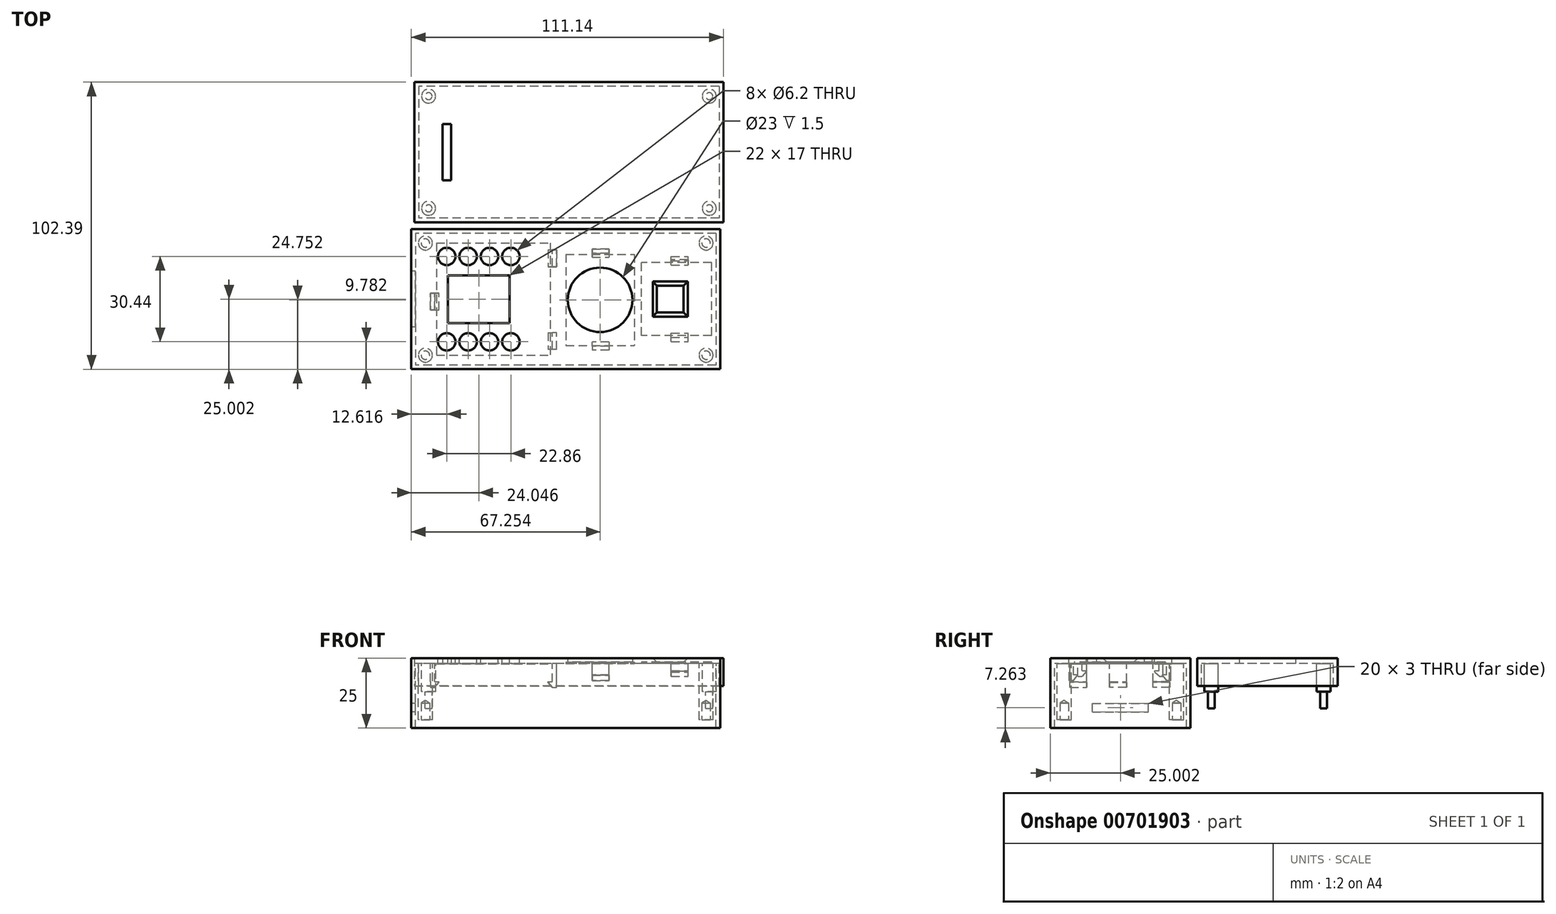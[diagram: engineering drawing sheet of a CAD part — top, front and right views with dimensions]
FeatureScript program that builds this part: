
annotation { "Feature Type Name" : "Feature", "Feature Type Description" : "" }
export const myFeature = defineFeature(function(context is Context, id is Id, definition is map)
    precondition{}
    {
        {
            var Q0;
            Q0=qCreatedBy(makeId("Top.planeOp"),FACE);
            var sketch = newSketch(context, id + "F0", { "sketchPlane" : qUnion([Q0])});
            skLineSegment(sketch, "E0.bottom", {"start": v(-49.7, 36.95) * mm, "end": v(60.3, 36.95) * mm});
            skLineSegment(sketch, "E0.top", {"start": v(-49.7, -13.05) * mm, "end": v(60.3, -13.05) * mm});
            skLineSegment(sketch, "E0.left", {"start": v(-49.7, 36.95) * mm, "end": v(-49.7, -13.05) * mm});
            skLineSegment(sketch, "E0.right", {"start": v(60.3, 36.95) * mm, "end": v(60.3, -13.05) * mm});
            skLineSegment(sketch, "E1.bottom", {"start": v(5.3, 27.95) * mm, "end": v(29.8, 27.95) * mm});
            skLineSegment(sketch, "E1.top", {"start": v(5.3, -4.55) * mm, "end": v(29.8, -4.55) * mm});
            skLineSegment(sketch, "E1.left", {"start": v(5.3, 27.95) * mm, "end": v(5.3, -4.55) * mm});
            skLineSegment(sketch, "E1.right", {"start": v(29.8, 27.95) * mm, "end": v(29.8, -4.55) * mm});
            skCircle(sketch, "E2", {"center": v(17.54, 11.7) * mm, "radius": 11.5 * mm});
            skLineSegment(sketch, "E3.top", {"start": v(38.3, 7.7) * mm, "end": v(46.8, 7.7) * mm});
            skLineSegment(sketch, "E4.bottom", {"start": v(38.3, 16.2) * mm, "end": v(46.8, 16.2) * mm});
            skLineSegment(sketch, "E4.left", {"start": v(38.3, 16.2) * mm, "end": v(38.3, 7.7) * mm});
            skLineSegment(sketch, "E4.right", {"start": v(46.8, 16.2) * mm, "end": v(46.8, 7.7) * mm});
            skPoint(sketch, "E5.orphan", {"position": v(-44.7, 36.95) * mm});
            skSolve(sketch);
        }
        {
            var Q0;
            Q0 = qSketchRegion(id + "F0", true);
            extrude(context, id + "F1", {"entities" : qUnion([Q0]), "depth" : 2 * mm, "offsetDistance" : 25 * mm});
        }
        {
            var Q0;
            Q0=qCreatedBy(makeId("Top.planeOp"),FACE);
            var sketch = newSketch(context, id + "F2", { "sketchPlane" : qUnion([Q0])});
            skLineSegment(sketch, "E6.bottom", {"start": v(-40.76, 31.95) * mm, "end": v(-0.26, 31.95) * mm});
            skLineSegment(sketch, "E6.top", {"start": v(-40.76, -8.05) * mm, "end": v(-0.26, -8.05) * mm});
            skLineSegment(sketch, "E6.left", {"start": v(-40.76, 31.95) * mm, "end": v(-40.76, -8.05) * mm});
            skLineSegment(sketch, "E6.right", {"start": v(-0.26, 31.95) * mm, "end": v(-0.26, -8.05) * mm});
            skCircle(sketch, "E7.MirrorC", {"center": v(-37.1, -3.27) * mm, "radius": 3.1 * mm});
            skLineSegment(sketch, "E8.bottom", {"start": v(-14.66, 20.45) * mm, "end": v(-14.66, 3.45) * mm});
            skLineSegment(sketch, "E8.top", {"start": v(-36.66, 20.45) * mm, "end": v(-36.66, 3.45) * mm});
            skLineSegment(sketch, "E8.left", {"start": v(-14.66, 20.45) * mm, "end": v(-36.66, 20.45) * mm});
            skLineSegment(sketch, "E8.right", {"start": v(-14.66, 3.45) * mm, "end": v(-36.66, 3.45) * mm});
            skPoint(sketch, "E9.orphan", {"position": v(-0.26, 11.95) * mm});
            skPoint(sketch, "E10.end.orphan", {"position": v(-40.76, 11.95) * mm});
            skCircle(sketch, "E11.1.0.0", {"center": v(-29.47, -3.27) * mm, "radius": 3.1 * mm});
            skCircle(sketch, "E11.2.0.0", {"center": v(-21.85, -3.27) * mm, "radius": 3.1 * mm});
            skCircle(sketch, "E11.3.0.0", {"center": v(-14.23, -3.27) * mm, "radius": 3.1 * mm});
            skLineSegment(sketch, "E11.direction1", {"start": v(-37.1, -3.27) * mm, "end": v(-29.47, -3.27) * mm, "construction": true});
            skCircle(sketch, "E12.MirrorC", {"center": v(-37.1, 27.17) * mm, "radius": 3.1 * mm});
            skCircle(sketch, "E13.1.0.0", {"center": v(-29.47, 27.17) * mm, "radius": 3.1 * mm});
            skCircle(sketch, "E13.2.0.0", {"center": v(-21.85, 27.17) * mm, "radius": 3.1 * mm});
            skCircle(sketch, "E13.3.0.0", {"center": v(-14.23, 27.17) * mm, "radius": 3.1 * mm});
            skLineSegment(sketch, "E13.direction1", {"start": v(-37.1, 27.17) * mm, "end": v(-29.47, 27.17) * mm, "construction": true});
            skSolve(sketch);
        }
        {
            var Q0;
            Q0 = qSketchRegion(id + "F2", true);
            extrude(context, id + "F3", {"entities" : qUnion([Q0]), "operationType" : NewBodyOperationType.ADD, "oppositeDirection" : true, "depth" : 0.1 * mm, "offsetDistance" : 25 * mm});
        }
        {
            var Q0;
            Q0=makeQuery(id+"F0.imprint","IMPRINT",FACE,{"disambiguationData":[TD([[makeQuery(id+"F0.imprint","IMPRINT",EDGE,{"derivedFrom":sQuery(id+"F0.wireOp",EDGE,"E1.bottom")}),-1.0]])]});
            extrude(context, id + "F4", {"entities" : qUnion([Q0]), "operationType" : NewBodyOperationType.ADD, "depth" : 2 * mm, "offsetDistance" : 25 * mm});
        }
        {
            var Q0;
            Q0=makeQuery(id+"F2.imprint","IMPRINT",FACE,{"disambiguationData":[TD([[makeQuery(id+"F2.imprint","IMPRINT",EDGE,{"derivedFrom":sQuery(id+"F2.wireOp",EDGE,"E8.bottom")}),-1.0]])]});
            extrude(context, id + "F5", {"entities" : qUnion([Q0]), "operationType" : NewBodyOperationType.REMOVE, "oppositeDirection" : true, "depth" : 5 * mm, "offsetDistance" : 25 * mm});
        }
        {
            var Q0;
            {var subQ0=sQuery(id+"F0.wireOp",EDGE,"E3.right");var subQ1=sQuery(id+"F0.wireOp",EDGE,"E3.left");var subQ2=sQuery(id+"F0.wireOp",EDGE,"E3.bottom");var subQ3=sQuery(id+"F0.wireOp",EDGE,"E1.right");var subQ4=sQuery(id+"F0.wireOp",EDGE,"E1.left");var subQ5=sQuery(id+"F0.wireOp",EDGE,"E1.top");var subQ6=sQuery(id+"F0.wireOp",EDGE,"E1.bottom");Q0=makeQuery(id+"FzuolDucDf3GuWk_4.boolean.opBoolean","MERGE",FACE,{"derivedFrom":[makeQuery(id+"F4.boolean.opBoolean","MERGE",FACE,{"derivedFrom":[makeQuery(id+"F1.opExtrude","CAP_FACE",FACE,{"disambiguationData":[OSD([sQuery(id+"F0.wireOp",EDGE,"E0.bottom"),sQuery(id+"F0.wireOp",EDGE,"E0.top"),sQuery(id+"F0.wireOp",EDGE,"E0.left"),sQuery(id+"F0.wireOp",EDGE,"E0.right"),subQ6,subQ5,subQ4,subQ3,subQ2,subQ1,subQ0,sQuery(id+"F0.wireOp",EDGE,"E3.top"),sQuery(id+"F0.wireOp",EDGE,"E4.left"),sQuery(id+"F0.wireOp",EDGE,"E4.right")])],"isStart":true}),makeQuery(id+"F4.opExtrude","CAP_FACE",FACE,{"disambiguationData":[OSD([subQ6,subQ5,subQ4,subQ3,sQuery(id+"F0.wireOp",EDGE,"E2")])],"isStart":true})]}),makeQuery(id+"FzuolDucDf3GuWk_4.opExtrude","CAP_FACE",FACE,{"disambiguationData":[OSD([subQ2,subQ1,subQ0,sQuery(id+"F0.wireOp",EDGE,"E4.bottom")])],"isStart":true})]});}
            var sketch = newSketch(context, id + "F6", { "sketchPlane" : qUnion([Q0])});
            skLineSegment(sketch, "E14.bottom", {"start": v(60.3, -36.95) * mm, "end": v(58.8, -36.95) * mm});
            skLineSegment(sketch, "E14.top", {"start": v(60.3, 13.05) * mm, "end": v(58.8, 13.05) * mm});
            skLineSegment(sketch, "E14.left", {"start": v(60.3, -36.95) * mm, "end": v(60.3, 13.05) * mm});
            skLineSegment(sketch, "E14.right", {"start": v(58.8, -36.95) * mm, "end": v(58.8, 13.05) * mm});
            skLineSegment(sketch, "E15.bottom", {"start": v(-49.7, -36.95) * mm, "end": v(-48.2, -36.95) * mm});
            skLineSegment(sketch, "E15.top", {"start": v(-49.7, 13.05) * mm, "end": v(-48.2, 13.05) * mm});
            skLineSegment(sketch, "E15.left", {"start": v(-49.7, -36.95) * mm, "end": v(-49.7, 13.05) * mm});
            skLineSegment(sketch, "E15.right", {"start": v(-48.2, -36.95) * mm, "end": v(-48.2, 13.05) * mm});
            skLineSegment(sketch, "E16.bottom", {"start": v(58.8, -36.95) * mm, "end": v(-48.2, -36.95) * mm});
            skLineSegment(sketch, "E16.top", {"start": v(58.8, -35.45) * mm, "end": v(-48.2, -35.45) * mm});
            skLineSegment(sketch, "E16.left", {"start": v(58.8, -36.95) * mm, "end": v(58.8, -35.45) * mm});
            skLineSegment(sketch, "E16.right", {"start": v(-48.2, -36.95) * mm, "end": v(-48.2, -35.45) * mm});
            skLineSegment(sketch, "E17.bottom", {"start": v(58.8, 13.05) * mm, "end": v(-48.2, 13.05) * mm});
            skLineSegment(sketch, "E17.top", {"start": v(58.8, 11.55) * mm, "end": v(-48.2, 11.55) * mm});
            skLineSegment(sketch, "E17.left", {"start": v(58.8, 13.05) * mm, "end": v(58.8, 11.55) * mm});
            skLineSegment(sketch, "E17.right", {"start": v(-48.2, 13.05) * mm, "end": v(-48.2, 11.55) * mm});
            skSolve(sketch);
        }
        {
            var Q0;
            Q0 = qSketchRegion(id + "F6", true);
            extrude(context, id + "F7", {"entities" : qUnion([Q0]), "operationType" : NewBodyOperationType.ADD, "depth" : 23 * mm, "offsetDistance" : 25 * mm});
        }
        {
            var Q0;
            Q0 = qSketchRegion(id + "F6", true);
            extrude(context, id + "F8", {"entities" : qUnion([Q0]), "operationType" : NewBodyOperationType.ADD, "depth" : 10 * mm, "offsetDistance" : 25 * mm});
        }
        {
            var Q0;
            Q0 = qSketchRegion(id + "F6", true);
            extrude(context, id + "F9", {"entities" : qUnion([Q0]), "operationType" : NewBodyOperationType.ADD, "depth" : 10 * mm, "offsetDistance" : 25 * mm});
        }
        {
            var Q0;
            Q0 = qSketchRegion(id + "F6", true);
            extrude(context, id + "F10", {"entities" : qUnion([Q0]), "operationType" : NewBodyOperationType.ADD, "depth" : 10 * mm, "offsetDistance" : 25 * mm});
        }
        {
            var Q0;
            {var subQ0=sQuery(id+"F0.wireOp",EDGE,"E3.right");var subQ1=sQuery(id+"F0.wireOp",EDGE,"E3.left");var subQ2=sQuery(id+"F0.wireOp",EDGE,"E3.bottom");var subQ3=sQuery(id+"F0.wireOp",EDGE,"E1.right");var subQ4=sQuery(id+"F0.wireOp",EDGE,"E1.left");var subQ5=sQuery(id+"F0.wireOp",EDGE,"E1.top");var subQ6=sQuery(id+"F0.wireOp",EDGE,"E1.bottom");Q0=makeQuery(id+"FzuolDucDf3GuWk_4.boolean.opBoolean","MERGE",FACE,{"derivedFrom":[makeQuery(id+"F4.boolean.opBoolean","MERGE",FACE,{"derivedFrom":[makeQuery(id+"F1.opExtrude","CAP_FACE",FACE,{"disambiguationData":[OSD([sQuery(id+"F0.wireOp",EDGE,"E0.bottom"),sQuery(id+"F0.wireOp",EDGE,"E0.top"),sQuery(id+"F0.wireOp",EDGE,"E0.left"),sQuery(id+"F0.wireOp",EDGE,"E0.right"),subQ6,subQ5,subQ4,subQ3,subQ2,subQ1,subQ0,sQuery(id+"F0.wireOp",EDGE,"E3.top"),sQuery(id+"F0.wireOp",EDGE,"E4.left"),sQuery(id+"F0.wireOp",EDGE,"E4.right")])],"isStart":true}),makeQuery(id+"F4.opExtrude","CAP_FACE",FACE,{"disambiguationData":[OSD([subQ6,subQ5,subQ4,subQ3,sQuery(id+"F0.wireOp",EDGE,"E2")])],"isStart":true})]}),makeQuery(id+"FzuolDucDf3GuWk_4.opExtrude","CAP_FACE",FACE,{"disambiguationData":[OSD([subQ2,subQ1,subQ0,sQuery(id+"F0.wireOp",EDGE,"E4.bottom")])],"isStart":true})]});}
            var sketch = newSketch(context, id + "F11", { "sketchPlane" : qUnion([Q0])});
            skLineSegment(sketch, "E18.bottom", {"start": v(42.85, -25.68) * mm, "end": v(48.85, -25.68) * mm});
            skLineSegment(sketch, "E18.top", {"start": v(42.85, -27.18) * mm, "end": v(48.85, -27.18) * mm});
            skLineSegment(sketch, "E18.left", {"start": v(42.85, -25.68) * mm, "end": v(42.85, -27.18) * mm});
            skLineSegment(sketch, "E18.right", {"start": v(48.85, -25.68) * mm, "end": v(48.85, -27.18) * mm});
            skLineSegment(sketch, "E19.bottom", {"start": v(14.73, -28.35) * mm, "end": v(20.73, -28.35) * mm});
            skLineSegment(sketch, "E19.top", {"start": v(14.73, -29.85) * mm, "end": v(20.73, -29.85) * mm});
            skLineSegment(sketch, "E19.left", {"start": v(14.73, -28.35) * mm, "end": v(14.73, -29.85) * mm});
            skLineSegment(sketch, "E19.right", {"start": v(20.73, -28.35) * mm, "end": v(20.73, -29.85) * mm});
            skLineSegment(sketch, "E20.bottom", {"start": v(42.85, 3.2) * mm, "end": v(48.85, 3.2) * mm});
            skLineSegment(sketch, "E20.top", {"start": v(42.85, 1.7) * mm, "end": v(48.85, 1.7) * mm});
            skLineSegment(sketch, "E20.left", {"start": v(42.85, 3.2) * mm, "end": v(42.85, 1.7) * mm});
            skLineSegment(sketch, "E20.right", {"start": v(48.85, 3.2) * mm, "end": v(48.85, 1.7) * mm});
            skSolve(sketch);
        }
        {
            var Q0;
            Q0=makeQuery(id+"F11.imprint","IMPRINT",FACE,{"disambiguationData":[TD([[makeQuery(id+"F11.imprint","IMPRINT",EDGE,{"derivedFrom":sQuery(id+"F11.wireOp",EDGE,"E18.bottom")}),-1.0]])]});
            extrude(context, id + "F12", {"entities" : qUnion([Q0]), "operationType" : NewBodyOperationType.ADD, "depth" : 2.5 * mm, "offsetDistance" : 25 * mm});
        }
        {
            var Q0;
            Q0=makeQuery(id+"F11.imprint","IMPRINT",FACE,{"disambiguationData":[TD([[makeQuery(id+"F11.imprint","IMPRINT",EDGE,{"derivedFrom":sQuery(id+"F11.wireOp",EDGE,"E19.bottom")}),-1.0]])]});
            extrude(context, id + "F13", {"entities" : qUnion([Q0]), "operationType" : NewBodyOperationType.ADD, "depth" : 4 * mm, "offsetDistance" : 25 * mm});
        }
        {
            var Q0;
            Q0=makeQuery(id+"F13.opExtrude","CAP_FACE",FACE,{"disambiguationData":[OSD([sQuery(id+"F11.wireOp",EDGE,"E19.bottom"),sQuery(id+"F11.wireOp",EDGE,"E19.top"),sQuery(id+"F11.wireOp",EDGE,"E19.left"),sQuery(id+"F11.wireOp",EDGE,"E19.right")])],"isStart":false});
            var sketch = newSketch(context, id + "F14", { "sketchPlane" : qUnion([Q0])});
            skLineSegment(sketch, "E21.bottom", {"start": v(14.73, -29.85) * mm, "end": v(20.73, -29.85) * mm});
            skLineSegment(sketch, "E21.top", {"start": v(14.73, -26.85) * mm, "end": v(20.73, -26.85) * mm});
            skLineSegment(sketch, "E21.left", {"start": v(14.73, -29.85) * mm, "end": v(14.73, -26.85) * mm});
            skLineSegment(sketch, "E21.right", {"start": v(20.73, -29.85) * mm, "end": v(20.73, -26.85) * mm});
            skSolve(sketch);
        }
        {
            var Q0;
            Q0 = qSketchRegion(id + "F14", true);
            extrude(context, id + "F15", {"entities" : qUnion([Q0]), "operationType" : NewBodyOperationType.ADD, "depth" : 2 * mm, "offsetDistance" : 25 * mm});
        }
        {
            var Q0;
            Q0=makeQuery(id+"F15.opExtrude","CAP_EDGE",EDGE,{"disambiguationData":[OSD([sQuery(id+"F14.wireOp",EDGE,"E21.top")])],"isStart":false});
            chamfer(context, id + "F16", {"entities" : qUnion([Q0]), "chamferType" : ChamferType.OFFSET_ANGLE, "width" : 1.5 * mm, "oppositeDirection" : true, "angle" : 50 * degree, "tangentPropagation" : true});
        }
        {
            var Q0;
            Q0=makeQuery(id+"F11.imprint","IMPRINT",FACE,{"disambiguationData":[TD([[makeQuery(id+"F11.imprint","IMPRINT",EDGE,{"derivedFrom":sQuery(id+"F11.wireOp",EDGE,"E18.bottom")}),1.0]])]});
            var sketch = newSketch(context, id + "F17", { "sketchPlane" : qUnion([Q0])});
            skLineSegment(sketch, "E22.bottom", {"start": v(2.04, 6) * mm, "end": v(2.04, 0) * mm});
            skLineSegment(sketch, "E22.top", {"start": v(0.54, 6) * mm, "end": v(0.54, 0) * mm});
            skLineSegment(sketch, "E22.left", {"start": v(2.04, 6) * mm, "end": v(0.54, 6) * mm});
            skLineSegment(sketch, "E22.right", {"start": v(2.04, 0) * mm, "end": v(0.54, 0) * mm});
            skLineSegment(sketch, "E23.bottom", {"start": v(20.72, 4.8) * mm, "end": v(14.72, 4.8) * mm});
            skLineSegment(sketch, "E23.top", {"start": v(20.72, 6.3) * mm, "end": v(14.72, 6.3) * mm});
            skLineSegment(sketch, "E23.left", {"start": v(20.72, 4.8) * mm, "end": v(20.72, 6.3) * mm});
            skLineSegment(sketch, "E23.right", {"start": v(14.72, 4.8) * mm, "end": v(14.72, 6.3) * mm});
            skLineSegment(sketch, "E24.bottom", {"start": v(-41.42, -8.1) * mm, "end": v(-41.42, -14.1) * mm});
            skLineSegment(sketch, "E24.top", {"start": v(-42.92, -8.1) * mm, "end": v(-42.92, -14.1) * mm});
            skLineSegment(sketch, "E24.left", {"start": v(-41.42, -8.1) * mm, "end": v(-42.92, -8.1) * mm});
            skLineSegment(sketch, "E24.right", {"start": v(-41.42, -14.1) * mm, "end": v(-42.92, -14.1) * mm});
            skLineSegment(sketch, "E25.top", {"start": v(20.67, 4.85) * mm, "end": v(14.67, 4.85) * mm});
            skLineSegment(sketch, "E26.top", {"start": v(20.76, 4.8) * mm, "end": v(14.76, 4.8) * mm});
            skLineSegment(sketch, "E27.bottom", {"start": v(2.04, -23.5) * mm, "end": v(2.04, -29.5) * mm});
            skLineSegment(sketch, "E27.top", {"start": v(0.54, -23.5) * mm, "end": v(0.54, -29.5) * mm});
            skLineSegment(sketch, "E27.left", {"start": v(2.04, -23.5) * mm, "end": v(0.54, -23.5) * mm});
            skLineSegment(sketch, "E27.right", {"start": v(2.04, -29.5) * mm, "end": v(0.54, -29.5) * mm});
            skSolve(sketch);
        }
        {
            var Q0;
            Q0=makeQuery(id+"F17.imprint","IMPRINT",FACE,{"disambiguationData":[TD([[makeQuery(id+"F17.imprint","IMPRINT",EDGE,{"derivedFrom":sQuery(id+"F17.wireOp",EDGE,"E22.bottom")}),-1.0]])]});
            extrude(context, id + "F18", {"entities" : qUnion([Q0]), "operationType" : NewBodyOperationType.ADD, "depth" : 6.5 * mm, "offsetDistance" : 25 * mm});
        }
        {
            var Q0;
            Q0=makeQuery(id+"F17.imprint","IMPRINT",FACE,{"disambiguationData":[TD([[makeQuery(id+"F17.imprint","IMPRINT",EDGE,{"derivedFrom":sQuery(id+"F17.wireOp",EDGE,"E24.bottom")}),-1.0]])]});
            extrude(context, id + "F19", {"entities" : qUnion([Q0]), "operationType" : NewBodyOperationType.ADD, "depth" : 6.5 * mm, "offsetDistance" : 25 * mm});
        }
        {
            var Q0;
            {var subQ0=sQuery(id+"F17.wireOp",EDGE,"E23.left");Q0=makeQuery(id+"F17.imprint","IMPRINT",FACE,{"disambiguationData":[TD([[makeQuery(id+"F17.imprint","IMPRINT",EDGE,{"derivedFrom":subQ0}),1.0]])]});}
            extrude(context, id + "F20", {"entities" : qUnion([Q0]), "operationType" : NewBodyOperationType.ADD, "depth" : 4 * mm, "offsetDistance" : 25 * mm});
        }
        {
            var Q0;
            Q0=makeQuery(id+"F20.opExtrude","CAP_FACE",FACE,{"disambiguationData":[OSD([sQuery(id+"F17.wireOp",EDGE,"E23.bottom"),sQuery(id+"F17.wireOp",EDGE,"E23.top"),sQuery(id+"F17.wireOp",EDGE,"E23.left"),sQuery(id+"F17.wireOp",EDGE,"E26.right")])],"isStart":false});
            var sketch = newSketch(context, id + "F21", { "sketchPlane" : qUnion([Q0])});
            skLineSegment(sketch, "E28.bottom", {"start": v(20.72, 3.3) * mm, "end": v(20.72, 6.3) * mm});
            skLineSegment(sketch, "E28.top", {"start": v(14.72, 3.3) * mm, "end": v(14.72, 6.3) * mm});
            skLineSegment(sketch, "E28.left", {"start": v(20.72, 3.3) * mm, "end": v(14.72, 3.3) * mm});
            skLineSegment(sketch, "E28.right", {"start": v(20.72, 6.3) * mm, "end": v(14.72, 6.3) * mm});
            skSolve(sketch);
        }
        {
            var Q0;
            Q0 = qSketchRegion(id + "F21", true);
            extrude(context, id + "F22", {"entities" : qUnion([Q0]), "operationType" : NewBodyOperationType.ADD, "depth" : 2 * mm, "offsetDistance" : 25 * mm});
        }
        {
            var Q0;
            Q0=makeQuery(id+"F22.opExtrude","CAP_EDGE",EDGE,{"disambiguationData":[OSD([sQuery(id+"F21.wireOp",EDGE,"E28.left")])],"isStart":false});
            chamfer(context, id + "F23", {"entities" : qUnion([Q0]), "chamferType" : ChamferType.OFFSET_ANGLE, "width" : 1.5 * mm, "oppositeDirection" : true, "angle" : 50 * degree, "tangentPropagation" : true});
        }
        {
            var Q0;
            Q0=makeQuery(id+"F18.opExtrude","CAP_FACE",FACE,{"disambiguationData":[OSD([sQuery(id+"F17.wireOp",EDGE,"E22.bottom"),sQuery(id+"F17.wireOp",EDGE,"E22.top"),sQuery(id+"F17.wireOp",EDGE,"E22.left"),sQuery(id+"F17.wireOp",EDGE,"E22.right")])],"isStart":false});
            var sketch = newSketch(context, id + "F24", { "sketchPlane" : qUnion([Q0])});
            skLineSegment(sketch, "E29.bottom", {"start": v(-0.96, 0) * mm, "end": v(2.04, 0) * mm});
            skLineSegment(sketch, "E29.top", {"start": v(-0.96, 6) * mm, "end": v(2.04, 6) * mm});
            skLineSegment(sketch, "E29.left", {"start": v(-0.96, 0) * mm, "end": v(-0.96, 6) * mm});
            skLineSegment(sketch, "E29.right", {"start": v(2.04, 0) * mm, "end": v(2.04, 6) * mm});
            skSolve(sketch);
        }
        {
            var Q0;
            Q0 = qSketchRegion(id + "F24", true);
            extrude(context, id + "F25", {"entities" : qUnion([Q0]), "operationType" : NewBodyOperationType.ADD, "depth" : 2 * mm, "offsetDistance" : 25 * mm});
        }
        {
            var Q0;
            Q0=makeQuery(id+"F25.opExtrude","CAP_EDGE",EDGE,{"disambiguationData":[OSD([sQuery(id+"F24.wireOp",EDGE,"E29.left")])],"isStart":false});
            chamfer(context, id + "F26", {"entities" : qUnion([Q0]), "chamferType" : ChamferType.OFFSET_ANGLE, "width" : 1.5 * mm, "oppositeDirection" : true, "angle" : 50 * degree, "tangentPropagation" : true});
        }
        {
            var Q0;
            Q0=makeQuery(id+"F19.opExtrude","CAP_FACE",FACE,{"disambiguationData":[OSD([sQuery(id+"F17.wireOp",EDGE,"E24.bottom"),sQuery(id+"F17.wireOp",EDGE,"E24.top"),sQuery(id+"F17.wireOp",EDGE,"E24.left"),sQuery(id+"F17.wireOp",EDGE,"E24.right")])],"isStart":false});
            var sketch = newSketch(context, id + "F27", { "sketchPlane" : qUnion([Q0])});
            skLineSegment(sketch, "E30.bottom", {"start": v(-42.92, -14.1) * mm, "end": v(-39.92, -14.1) * mm});
            skLineSegment(sketch, "E30.top", {"start": v(-42.92, -8.1) * mm, "end": v(-39.92, -8.1) * mm});
            skLineSegment(sketch, "E30.left", {"start": v(-42.92, -14.1) * mm, "end": v(-42.92, -8.1) * mm});
            skLineSegment(sketch, "E30.right", {"start": v(-39.92, -14.1) * mm, "end": v(-39.92, -8.1) * mm});
            skSolve(sketch);
        }
        {
            var Q0;
            Q0 = qSketchRegion(id + "F27", true);
            extrude(context, id + "F28", {"entities" : qUnion([Q0]), "operationType" : NewBodyOperationType.ADD, "depth" : 2 * mm, "offsetDistance" : 25 * mm});
        }
        {
            var Q0;
            Q0=makeQuery(id+"F28.opExtrude","CAP_EDGE",EDGE,{"disambiguationData":[OSD([sQuery(id+"F27.wireOp",EDGE,"E30.right")])],"isStart":false});
            chamfer(context, id + "F29", {"entities" : qUnion([Q0]), "chamferType" : ChamferType.OFFSET_ANGLE, "width" : 1.5 * mm, "oppositeDirection" : false, "angle" : 50 * degree, "tangentPropagation" : true});
        }
        {
            var Q0;
            {var subQ0=sQuery(id+"F0.wireOp",EDGE,"E3.right");var subQ1=sQuery(id+"F0.wireOp",EDGE,"E3.left");var subQ2=sQuery(id+"F0.wireOp",EDGE,"E3.bottom");var subQ3=sQuery(id+"F0.wireOp",EDGE,"E1.right");var subQ4=sQuery(id+"F0.wireOp",EDGE,"E1.left");var subQ5=sQuery(id+"F0.wireOp",EDGE,"E1.top");var subQ6=sQuery(id+"F0.wireOp",EDGE,"E1.bottom");Q0=makeQuery(id+"FzuolDucDf3GuWk_4.boolean.opBoolean","MERGE",FACE,{"derivedFrom":[makeQuery(id+"F4.boolean.opBoolean","MERGE",FACE,{"derivedFrom":[makeQuery(id+"F1.opExtrude","CAP_FACE",FACE,{"disambiguationData":[OSD([sQuery(id+"F0.wireOp",EDGE,"E0.bottom"),sQuery(id+"F0.wireOp",EDGE,"E0.top"),sQuery(id+"F0.wireOp",EDGE,"E0.left"),sQuery(id+"F0.wireOp",EDGE,"E0.right"),subQ6,subQ5,subQ4,subQ3,subQ2,subQ1,subQ0,sQuery(id+"F0.wireOp",EDGE,"E3.top"),sQuery(id+"F0.wireOp",EDGE,"E4.left"),sQuery(id+"F0.wireOp",EDGE,"E4.right")])],"isStart":true}),makeQuery(id+"F4.opExtrude","CAP_FACE",FACE,{"disambiguationData":[OSD([subQ6,subQ5,subQ4,subQ3,sQuery(id+"F0.wireOp",EDGE,"E2")])],"isStart":true})]}),makeQuery(id+"FzuolDucDf3GuWk_4.opExtrude","CAP_FACE",FACE,{"disambiguationData":[OSD([subQ2,subQ1,subQ0,sQuery(id+"F0.wireOp",EDGE,"E4.bottom")])],"isStart":true})]});}
            var sketch = newSketch(context, id + "F30", { "sketchPlane" : qUnion([Q0])});
            skCircle(sketch, "E31", {"center": v(-44.7, 8.05) * mm, "radius": 2.5 * mm});
            skCircle(sketch, "E32", {"center": v(-44.7, -31.95) * mm, "radius": 2.5 * mm});
            skCircle(sketch, "E33", {"center": v(55.3, -31.95) * mm, "radius": 2.5 * mm});
            skCircle(sketch, "E34", {"center": v(55.3, 8.05) * mm, "radius": 2.5 * mm});
            skSolve(sketch);
        }
        {
            var Q0;
            Q0=makeQuery(id+"F30.imprint","IMPRINT",FACE,{"disambiguationData":[TD([[makeQuery(id+"F30.imprint","IMPRINT",EDGE,{"derivedFrom":sQuery(id+"F30.wireOp",EDGE,"E31")}),1.0]])]});
            var Q1;
            Q1=makeQuery(id+"F30.imprint","IMPRINT",FACE,{"disambiguationData":[TD([[makeQuery(id+"F30.imprint","IMPRINT",EDGE,{"derivedFrom":sQuery(id+"F30.wireOp",EDGE,"E32")}),1.0]])]});
            var Q2;
            Q2=makeQuery(id+"F30.imprint","IMPRINT",FACE,{"disambiguationData":[TD([[makeQuery(id+"F30.imprint","IMPRINT",EDGE,{"derivedFrom":sQuery(id+"F30.wireOp",EDGE,"E34")}),1.0]])]});
            var Q3;
            Q3=makeQuery(id+"F30.imprint","IMPRINT",FACE,{"disambiguationData":[TD([[makeQuery(id+"F30.imprint","IMPRINT",EDGE,{"derivedFrom":sQuery(id+"F30.wireOp",EDGE,"E33")}),1.0]])]});
            extrude(context, id + "F31", {"entities" : qUnion([Q0, Q1, Q2, Q3]), "operationType" : NewBodyOperationType.ADD, "depth" : 20 * mm, "offsetDistance" : 25 * mm});
        }
        {
            var Q0;
            Q0=makeQuery(id+"F31.opExtrude","CAP_FACE",FACE,{"disambiguationData":[OSD([sQuery(id+"F30.wireOp",EDGE,"E31")])],"isStart":false});
            var sketch = newSketch(context, id + "F32", { "sketchPlane" : qUnion([Q0])});
            skCircle(sketch, "E35", {"center": v(55.3, 8.05) * mm, "radius": 1.5 * mm});
            skCircle(sketch, "E36", {"center": v(55.3, -31.95) * mm, "radius": 1.5 * mm});
            skCircle(sketch, "E37", {"center": v(-44.7, -31.95) * mm, "radius": 1.5 * mm});
            skCircle(sketch, "E38", {"center": v(-44.7, 8.05) * mm, "radius": 1.5 * mm});
            skSolve(sketch);
        }
        {
            var Q0;
            Q0=sQuery(id+"F32.wireOp",VERTEX,"E38.center");
            var Q1;
            Q1=sQuery(id+"F32.wireOp",VERTEX,"E37.center");
            var Q2;
            Q2=sQuery(id+"F32.wireOp",VERTEX,"E35.center");
            var Q3;
            Q3=sQuery(id+"F32.wireOp",VERTEX,"E36.center");
            var Q4;
            Q4=makeQuery(id+"F1.opExtrude","SWEPT_BODY",BODY,{"disambiguationData":[OSD([sQuery(id+"F0.wireOp",EDGE,"E0.bottom"),sQuery(id+"F0.wireOp",EDGE,"E0.top"),sQuery(id+"F0.wireOp",EDGE,"E0.left"),sQuery(id+"F0.wireOp",EDGE,"E0.right"),sQuery(id+"F0.wireOp",EDGE,"E1.bottom"),sQuery(id+"F0.wireOp",EDGE,"E1.top"),sQuery(id+"F0.wireOp",EDGE,"E1.left"),sQuery(id+"F0.wireOp",EDGE,"E1.right"),sQuery(id+"F0.wireOp",EDGE,"E3.bottom"),sQuery(id+"F0.wireOp",EDGE,"E3.left"),sQuery(id+"F0.wireOp",EDGE,"E3.right"),sQuery(id+"F0.wireOp",EDGE,"E3.top"),sQuery(id+"F0.wireOp",EDGE,"E4.left"),sQuery(id+"F0.wireOp",EDGE,"E4.right")])]});
            hole(context, id + "F33", {"style" : HoleStyle.SIMPLE, "endStyle" : HoleEndStyle.BLIND, "holeDiameter" : 3 * mm, "majorDiameter" : 5 * mm, "holeDepth" : 6 * mm, "isTappedThrough" : true, "tappedDepth" : 12 * mm, "tapClearance" : 3, "startFromSketch" : true, "locations" : qUnion([Q0, Q1, Q2, Q3]), "scope" : qUnion([Q4])});
        }
        {
            var Q0;
            Q0=qCreatedBy(makeId("Top.planeOp"),FACE);
            var sketch = newSketch(context, id + "F34", { "sketchPlane" : qUnion([Q0])});
            skLineSegment(sketch, "E39.bottom", {"start": v(-48.57, 89.34) * mm, "end": v(61.43, 89.34) * mm});
            skLineSegment(sketch, "E39.top", {"start": v(-48.57, 39.34) * mm, "end": v(61.43, 39.34) * mm});
            skLineSegment(sketch, "E39.left", {"start": v(-48.57, 89.34) * mm, "end": v(-48.57, 39.34) * mm});
            skLineSegment(sketch, "E39.right", {"start": v(61.43, 89.34) * mm, "end": v(61.43, 39.34) * mm});
            skPoint(sketch, "E40.orphan", {"position": v(-42.5, 89.34) * mm});
            skSolve(sketch);
        }
        {
            var Q0;
            Q0 = qSketchRegion(id + "F34", true);
            extrude(context, id + "F35", {"entities" : qUnion([Q0]), "depth" : 2 * mm, "offsetDistance" : 25 * mm});
        }
        {
            var Q0;
            Q0=makeQuery(id+"F35.opExtrude","CAP_FACE",FACE,{"disambiguationData":[OSD([sQuery(id+"F34.wireOp",EDGE,"E39.bottom"),sQuery(id+"F34.wireOp",EDGE,"E39.top"),sQuery(id+"F34.wireOp",EDGE,"E39.left"),sQuery(id+"F34.wireOp",EDGE,"E39.right")])],"isStart":true});
            var sketch = newSketch(context, id + "F36", { "sketchPlane" : qUnion([Q0])});
            skLineSegment(sketch, "E41.bottom", {"start": v(61.43, -89.34) * mm, "end": v(59.93, -89.34) * mm});
            skLineSegment(sketch, "E41.top", {"start": v(61.43, -39.34) * mm, "end": v(59.93, -39.34) * mm});
            skLineSegment(sketch, "E41.left", {"start": v(61.43, -89.34) * mm, "end": v(61.43, -39.34) * mm});
            skLineSegment(sketch, "E41.right", {"start": v(59.93, -89.34) * mm, "end": v(59.93, -39.34) * mm});
            skLineSegment(sketch, "E42.bottom", {"start": v(-48.57, -89.34) * mm, "end": v(-47.07, -89.34) * mm});
            skLineSegment(sketch, "E42.top", {"start": v(-48.57, -39.34) * mm, "end": v(-47.07, -39.34) * mm});
            skLineSegment(sketch, "E42.left", {"start": v(-48.57, -89.34) * mm, "end": v(-48.57, -39.34) * mm});
            skLineSegment(sketch, "E42.right", {"start": v(-47.07, -89.34) * mm, "end": v(-47.07, -39.34) * mm});
            skLineSegment(sketch, "E43.bottom", {"start": v(59.93, -89.34) * mm, "end": v(-47.07, -89.34) * mm});
            skLineSegment(sketch, "E43.top", {"start": v(59.93, -87.84) * mm, "end": v(-47.07, -87.84) * mm});
            skLineSegment(sketch, "E43.left", {"start": v(59.93, -89.34) * mm, "end": v(59.93, -87.84) * mm});
            skLineSegment(sketch, "E43.right", {"start": v(-47.07, -89.34) * mm, "end": v(-47.07, -87.84) * mm});
            skLineSegment(sketch, "E44.bottom", {"start": v(59.93, -39.34) * mm, "end": v(-47.07, -39.34) * mm});
            skLineSegment(sketch, "E44.top", {"start": v(59.93, -40.84) * mm, "end": v(-47.07, -40.84) * mm});
            skLineSegment(sketch, "E44.left", {"start": v(59.93, -39.34) * mm, "end": v(59.93, -40.84) * mm});
            skLineSegment(sketch, "E44.right", {"start": v(-47.07, -39.34) * mm, "end": v(-47.07, -40.84) * mm});
            skSolve(sketch);
        }
        {
            var Q0;
            Q0 = qSketchRegion(id + "F36", true);
            extrude(context, id + "F37", {"entities" : qUnion([Q0]), "operationType" : NewBodyOperationType.ADD, "depth" : 8 * mm, "offsetDistance" : 25 * mm});
        }
        {
            var Q0;
            Q0=makeQuery(id+"F35.opExtrude","CAP_FACE",FACE,{"disambiguationData":[OSD([sQuery(id+"F34.wireOp",EDGE,"E39.bottom"),sQuery(id+"F34.wireOp",EDGE,"E39.top"),sQuery(id+"F34.wireOp",EDGE,"E39.left"),sQuery(id+"F34.wireOp",EDGE,"E39.right")])],"isStart":true});
            var sketch = newSketch(context, id + "F38", { "sketchPlane" : qUnion([Q0])});
            skCircle(sketch, "E45", {"center": v(-43.57, -84.34) * mm, "radius": 2.5 * mm});
            skCircle(sketch, "E46", {"center": v(-43.57, -44.34) * mm, "radius": 2.5 * mm});
            skCircle(sketch, "E47", {"center": v(56.43, -44.34) * mm, "radius": 2.5 * mm});
            skCircle(sketch, "E48", {"center": v(56.43, -84.34) * mm, "radius": 2.5 * mm});
            skSolve(sketch);
        }
        {
            var Q0;
            Q0=makeQuery(id+"F38.imprint","IMPRINT",FACE,{"disambiguationData":[TD([[makeQuery(id+"F38.imprint","IMPRINT",EDGE,{"derivedFrom":sQuery(id+"F38.wireOp",EDGE,"E48")}),1.0]])]});
            var Q1;
            Q1=makeQuery(id+"F38.imprint","IMPRINT",FACE,{"disambiguationData":[TD([[makeQuery(id+"F38.imprint","IMPRINT",EDGE,{"derivedFrom":sQuery(id+"F38.wireOp",EDGE,"E47")}),1.0]])]});
            var Q2;
            Q2=makeQuery(id+"F38.imprint","IMPRINT",FACE,{"disambiguationData":[TD([[makeQuery(id+"F38.imprint","IMPRINT",EDGE,{"derivedFrom":sQuery(id+"F38.wireOp",EDGE,"E46")}),1.0]])]});
            var Q3;
            Q3=makeQuery(id+"F38.imprint","IMPRINT",FACE,{"disambiguationData":[TD([[makeQuery(id+"F38.imprint","IMPRINT",EDGE,{"derivedFrom":sQuery(id+"F38.wireOp",EDGE,"E45")}),1.0]])]});
            extrude(context, id + "F39", {"entities" : qUnion([Q0, Q1, Q2, Q3]), "operationType" : NewBodyOperationType.ADD, "depth" : 10 * mm, "offsetDistance" : 25 * mm});
        }
        {
            var Q0;
            Q0=makeQuery(id+"F39.opExtrude","CAP_FACE",FACE,{"disambiguationData":[OSD([sQuery(id+"F38.wireOp",EDGE,"E46")])],"isStart":false});
            var sketch = newSketch(context, id + "F40", { "sketchPlane" : qUnion([Q0])});
            skCircle(sketch, "E49", {"center": v(-43.57, -44.34) * mm, "radius": 1.25 * mm});
            skCircle(sketch, "E50", {"center": v(-43.57, -84.34) * mm, "radius": 1.25 * mm});
            skCircle(sketch, "E51", {"center": v(56.43, -84.34) * mm, "radius": 1.25 * mm});
            skCircle(sketch, "E52", {"center": v(56.43, -44.34) * mm, "radius": 1.25 * mm});
            skSolve(sketch);
        }
        {
            var Q0;
            Q0=makeQuery(id+"F40.imprint","IMPRINT",FACE,{"disambiguationData":[TD([[makeQuery(id+"F40.imprint","IMPRINT",EDGE,{"derivedFrom":sQuery(id+"F40.wireOp",EDGE,"E50")}),1.0]])]});
            var Q1;
            Q1=makeQuery(id+"F40.imprint","IMPRINT",FACE,{"disambiguationData":[TD([[makeQuery(id+"F40.imprint","IMPRINT",EDGE,{"derivedFrom":sQuery(id+"F40.wireOp",EDGE,"E51")}),1.0]])]});
            var Q2;
            Q2=makeQuery(id+"F40.imprint","IMPRINT",FACE,{"disambiguationData":[TD([[makeQuery(id+"F40.imprint","IMPRINT",EDGE,{"derivedFrom":sQuery(id+"F40.wireOp",EDGE,"E52")}),1.0]])]});
            var Q3;
            Q3=makeQuery(id+"F40.imprint","IMPRINT",FACE,{"disambiguationData":[TD([[makeQuery(id+"F40.imprint","IMPRINT",EDGE,{"derivedFrom":sQuery(id+"F40.wireOp",EDGE,"E49")}),1.0]])]});
            var Q4;
            Q4=sQuery(id+"F40.wireOp",EDGE,"E49");
            var Q5;
            Q5=sQuery(id+"F40.wireOp",EDGE,"E50");
            var Q6;
            Q6=sQuery(id+"F40.wireOp",EDGE,"E51");
            var Q7;
            Q7=sQuery(id+"F40.wireOp",EDGE,"E52");
            extrude(context, id + "F41", {"entities" : qUnion([Q0, Q1, Q2, Q3]), "operationType" : NewBodyOperationType.ADD, "surfaceEntities" : qUnion([Q4, Q5, Q6, Q7]), "depth" : 6 * mm, "offsetDistance" : 25 * mm});
        }
        {
            var Q0;
            Q0=makeQuery(id+"F35.opExtrude","CAP_FACE",FACE,{"disambiguationData":[OSD([sQuery(id+"F34.wireOp",EDGE,"E39.bottom"),sQuery(id+"F34.wireOp",EDGE,"E39.top"),sQuery(id+"F34.wireOp",EDGE,"E39.left"),sQuery(id+"F34.wireOp",EDGE,"E39.right")])],"isStart":true});
            var sketch = newSketch(context, id + "F42", { "sketchPlane" : qUnion([Q0])});
            skLineSegment(sketch, "E53.bottom", {"start": v(-38.57, -74.34) * mm, "end": v(-38.57, -54.34) * mm});
            skLineSegment(sketch, "E53.top", {"start": v(-35.57, -74.34) * mm, "end": v(-35.57, -54.34) * mm});
            skLineSegment(sketch, "E53.left", {"start": v(-38.57, -74.34) * mm, "end": v(-35.57, -74.34) * mm});
            skLineSegment(sketch, "E53.right", {"start": v(-38.57, -54.34) * mm, "end": v(-35.57, -54.34) * mm});
            skSolve(sketch);
        }
        {
            var Q0;
            Q0 = qSketchRegion(id + "F42", true);
            extrude(context, id + "F43", {"entities" : qUnion([Q0]), "operationType" : NewBodyOperationType.REMOVE, "flatOperationType" : FlatOperationType.REMOVE, "endBound" : BoundingType.THROUGH_ALL, "oppositeDirection" : true, "depth" : 10 * mm, "offsetDistance" : 25 * mm, "domain" : OperationDomain.MODEL});
        }
        {
            var Q0;
            Q0=makeQuery(id+"F35.opExtrude","CAP_FACE",FACE,{"disambiguationData":[OSD([sQuery(id+"F34.wireOp",EDGE,"E39.bottom"),sQuery(id+"F34.wireOp",EDGE,"E39.top"),sQuery(id+"F34.wireOp",EDGE,"E39.left"),sQuery(id+"F34.wireOp",EDGE,"E39.right")])],"isStart":true});
            var sketch = newSketch(context, id + "F44", { "sketchPlane" : qUnion([Q0])});
            skCircle(sketch, "E54", {"center": v(-28.57, -64.34) * mm, "radius": 2.5 * mm});
            skCircle(sketch, "E55", {"center": v(-13.57, -64.34) * mm, "radius": 2.5 * mm});
            skCircle(sketch, "E56", {"center": v(17.43, -64.34) * mm, "radius": 2.5 * mm});
            skCircle(sketch, "E57", {"center": v(43.43, -64.34) * mm, "radius": 2.5 * mm});
            skSolve(sketch);
        }
        {
            var Q0;
            Q0=makeQuery(id+"F1.opExtrude","CAP_EDGE",EDGE,{"disambiguationData":[OSD([sQuery(id+"F0.wireOp",EDGE,"E4.right")])],"isStart":false});
            var Q1;
            Q1=makeQuery(id+"F1.opExtrude","CAP_EDGE",EDGE,{"disambiguationData":[OSD([sQuery(id+"F0.wireOp",EDGE,"E3.top")])],"isStart":false});
            var Q2;
            Q2=makeQuery(id+"F1.opExtrude","CAP_EDGE",EDGE,{"disambiguationData":[OSD([sQuery(id+"F0.wireOp",EDGE,"E4.left")])],"isStart":false});
            var Q3;
            Q3=makeQuery(id+"F1.opExtrude","CAP_EDGE",EDGE,{"disambiguationData":[OSD([sQuery(id+"F0.wireOp",EDGE,"E4.bottom")])],"isStart":false});
            chamfer(context, id + "F45", {"entities" : qUnion([Q0, Q1, Q2, Q3]), "width" : 2 * mm, "tangentPropagation" : true});
        }
        {
            var Q0;
            Q0=makeQuery(id+"F2.imprint","IMPRINT",FACE,{"disambiguationData":[TD([[makeQuery(id+"F2.imprint","IMPRINT",EDGE,{"derivedFrom":sQuery(id+"F2.wireOp",EDGE,"E7.MirrorC")}),1.0]])]});
            var Q1;
            Q1=makeQuery(id+"F2.imprint","IMPRINT",FACE,{"disambiguationData":[TD([[makeQuery(id+"F2.imprint","IMPRINT",EDGE,{"derivedFrom":sQuery(id+"F2.wireOp",EDGE,"E11.1.0.0")}),1.0]])]});
            var Q2;
            Q2=makeQuery(id+"F2.imprint","IMPRINT",FACE,{"disambiguationData":[TD([[makeQuery(id+"F2.imprint","IMPRINT",EDGE,{"derivedFrom":sQuery(id+"F2.wireOp",EDGE,"E11.2.0.0")}),1.0]])]});
            var Q3;
            Q3=makeQuery(id+"F2.imprint","IMPRINT",FACE,{"disambiguationData":[TD([[makeQuery(id+"F2.imprint","IMPRINT",EDGE,{"derivedFrom":sQuery(id+"F2.wireOp",EDGE,"E11.3.0.0")}),1.0]])]});
            var Q4;
            Q4=makeQuery(id+"F2.imprint","IMPRINT",FACE,{"disambiguationData":[TD([[makeQuery(id+"F2.imprint","IMPRINT",EDGE,{"derivedFrom":sQuery(id+"F2.wireOp",EDGE,"E13.3.0.0")}),1.0]])]});
            var Q5;
            Q5=makeQuery(id+"F2.imprint","IMPRINT",FACE,{"disambiguationData":[TD([[makeQuery(id+"F2.imprint","IMPRINT",EDGE,{"derivedFrom":sQuery(id+"F2.wireOp",EDGE,"E13.2.0.0")}),1.0]])]});
            var Q6;
            Q6=makeQuery(id+"F2.imprint","IMPRINT",FACE,{"disambiguationData":[TD([[makeQuery(id+"F2.imprint","IMPRINT",EDGE,{"derivedFrom":sQuery(id+"F2.wireOp",EDGE,"E13.1.0.0")}),1.0]])]});
            var Q7;
            Q7=makeQuery(id+"F2.imprint","IMPRINT",FACE,{"disambiguationData":[TD([[makeQuery(id+"F2.imprint","IMPRINT",EDGE,{"derivedFrom":sQuery(id+"F2.wireOp",EDGE,"E12.MirrorC")}),1.0]])]});
            extrude(context, id + "F46", {"entities" : qUnion([Q0, Q1, Q2, Q3, Q4, Q5, Q6, Q7]), "operationType" : NewBodyOperationType.REMOVE, "depth" : 5 * mm, "offsetDistance" : 25 * mm});
        }
        {
            var Q0;
            Q0=makeQuery(id+"F3.boolean.opBoolean","SPLIT",FACE,{"disambiguationData":[TD([makeQuery(id+"F3.opExtrude","SWEPT_FACE",FACE,{"disambiguationData":[OSD([sQuery(id+"F2.wireOp",EDGE,"E8.bottom")])]})])],"derivedFrom":makeQuery(id+"F1.opExtrude","CAP_FACE",FACE,{"disambiguationData":[OSD([sQuery(id+"F0.wireOp",EDGE,"E0.bottom"),sQuery(id+"F0.wireOp",EDGE,"E0.top"),sQuery(id+"F0.wireOp",EDGE,"E0.left"),sQuery(id+"F0.wireOp",EDGE,"E0.right"),sQuery(id+"F0.wireOp",EDGE,"E1.bottom"),sQuery(id+"F0.wireOp",EDGE,"E1.top"),sQuery(id+"F0.wireOp",EDGE,"E1.left"),sQuery(id+"F0.wireOp",EDGE,"E1.right"),sQuery(id+"F0.wireOp",EDGE,"E4.bottom"),sQuery(id+"F0.wireOp",EDGE,"E3.top"),sQuery(id+"F0.wireOp",EDGE,"E4.left"),sQuery(id+"F0.wireOp",EDGE,"E4.right")])],"isStart":true})});
            extrude(context, id + "F47", {"entities" : qUnion([Q0]), "operationType" : NewBodyOperationType.REMOVE, "oppositeDirection" : true, "depth" : 5 * mm, "offsetDistance" : 25 * mm});
        }
        {
            var Q0;
            Q0=makeQuery(id+"F7.boolean.opBoolean","MERGE",FACE,{"derivedFrom":[makeQuery(id+"F1.opExtrude","SWEPT_FACE",FACE,{"disambiguationData":[OSD([sQuery(id+"F0.wireOp",EDGE,"E0.left")])]}),makeQuery(id+"F7.opExtrude","SWEPT_FACE",FACE,{"disambiguationData":[OSD([sQuery(id+"F6.wireOp",EDGE,"E15.left")])]})]});
            var sketch = newSketch(context, id + "F48", { "sketchPlane" : qUnion([Q0])});
            skLineSegment(sketch, "E58.bottom", {"start": v(-1.95, -17.24) * mm, "end": v(-21.95, -17.24) * mm});
            skLineSegment(sketch, "E58.top", {"start": v(-1.95, -14.24) * mm, "end": v(-21.95, -14.24) * mm});
            skLineSegment(sketch, "E58.left", {"start": v(-1.95, -17.24) * mm, "end": v(-1.95, -14.24) * mm});
            skLineSegment(sketch, "E58.right", {"start": v(-21.95, -17.24) * mm, "end": v(-21.95, -14.24) * mm});
            skSolve(sketch);
        }
        {
            var Q0;
            Q0=makeQuery(id+"F0.imprint","IMPRINT",FACE,{"disambiguationData":[TD([[makeQuery(id+"F0.imprint","IMPRINT",EDGE,{"derivedFrom":sQuery(id+"F0.wireOp",EDGE,"E1.bottom")}),-1.0]])]});
            extrude(context, id + "F49", {"entities" : qUnion([Q0]), "operationType" : NewBodyOperationType.REMOVE, "depth" : 0.5 * mm, "offsetDistance" : 25 * mm});
        }
        {
            var Q0;
            {var subQ0=sQuery(id+"F0.wireOp",EDGE,"E1.right");var subQ1=sQuery(id+"F0.wireOp",EDGE,"E1.left");var subQ2=sQuery(id+"F0.wireOp",EDGE,"E1.top");var subQ3=sQuery(id+"F0.wireOp",EDGE,"E1.bottom");var subQ4=sQuery(id+"F0.wireOp",EDGE,"E4.bottom");var subQ5=sQuery(id+"F0.wireOp",EDGE,"E3.top");var subQ6=sQuery(id+"F0.wireOp",EDGE,"E0.bottom");var subQ7=sQuery(id+"F0.wireOp",EDGE,"E0.right");var subQ8=sQuery(id+"F0.wireOp",EDGE,"E0.top");var subQ9=sQuery(id+"F0.wireOp",EDGE,"E0.left");var subQ10=sQuery(id+"F0.wireOp",EDGE,"E4.left");var subQ11=sQuery(id+"F0.wireOp",EDGE,"E4.right");Q0=makeQuery(id+"F4.boolean.opBoolean","MERGE",FACE,{"derivedFrom":[makeQuery(id+"F3.boolean.opBoolean","SPLIT",FACE,{"disambiguationData":[TD([makeQuery(id+"F1.opExtrude","SWEPT_FACE",FACE,{"disambiguationData":[OSD([subQ6])]})])],"derivedFrom":makeQuery(id+"F1.opExtrude","CAP_FACE",FACE,{"disambiguationData":[OSD([subQ6,subQ8,subQ9,subQ7,subQ3,subQ2,subQ1,subQ0,subQ4,subQ5,subQ10,subQ11])],"isStart":true})}),makeQuery(id+"F4.opExtrude","CAP_FACE",FACE,{"disambiguationData":[OSD([subQ3,subQ2,subQ1,subQ0,sQuery(id+"F0.wireOp",EDGE,"E2")])],"isStart":true})]});}
            var sketch = newSketch(context, id + "F50", { "sketchPlane" : qUnion([Q0])});
            skLineSegment(sketch, "E59.bottom", {"start": v(57.3, 1.05) * mm, "end": v(57.3, -24.95) * mm});
            skLineSegment(sketch, "E59.top", {"start": v(32.3, 1.05) * mm, "end": v(32.3, -24.95) * mm});
            skLineSegment(sketch, "E59.left", {"start": v(57.3, 1.05) * mm, "end": v(32.3, 1.05) * mm});
            skLineSegment(sketch, "E59.right", {"start": v(57.3, -24.95) * mm, "end": v(32.3, -24.95) * mm});
            skSolve(sketch);
        }
        {
            var Q0;
            Q0=makeQuery(id+"F50.imprint","IMPRINT",FACE,{"disambiguationData":[TD([[makeQuery(id+"F50.imprint","IMPRINT",EDGE,{"derivedFrom":sQuery(id+"F50.wireOp",EDGE,"E59.bottom")}),-1.0]])]});
            extrude(context, id + "F51", {"entities" : qUnion([Q0]), "operationType" : NewBodyOperationType.REMOVE, "oppositeDirection" : true, "depth" : 0.5 * mm, "offsetDistance" : 25 * mm});
        }
        {
            var Q0;
            Q0=makeQuery(id+"F11.imprint","IMPRINT",FACE,{"disambiguationData":[TD([[makeQuery(id+"F11.imprint","IMPRINT",EDGE,{"derivedFrom":sQuery(id+"F11.wireOp",EDGE,"E20.bottom")}),-1.0]])]});
            extrude(context, id + "F52", {"entities" : qUnion([Q0]), "operationType" : NewBodyOperationType.ADD, "depth" : 2.5 * mm, "offsetDistance" : 25 * mm});
        }
        {
            var Q0;
            Q0=makeQuery(id+"F52.opExtrude","CAP_FACE",FACE,{"disambiguationData":[OSD([sQuery(id+"F11.wireOp",EDGE,"E20.bottom"),sQuery(id+"F11.wireOp",EDGE,"E20.top"),sQuery(id+"F11.wireOp",EDGE,"E20.left"),sQuery(id+"F11.wireOp",EDGE,"E20.right")])],"isStart":false});
            var sketch = newSketch(context, id + "F53", { "sketchPlane" : qUnion([Q0])});
            skLineSegment(sketch, "E60.bottom", {"start": v(42.85, 3.2) * mm, "end": v(48.85, 3.2) * mm});
            skLineSegment(sketch, "E60.top", {"start": v(42.85, 0.2) * mm, "end": v(48.85, 0.2) * mm});
            skLineSegment(sketch, "E60.left", {"start": v(42.85, 3.2) * mm, "end": v(42.85, 0.2) * mm});
            skLineSegment(sketch, "E60.right", {"start": v(48.85, 3.2) * mm, "end": v(48.85, 0.2) * mm});
            skLineSegment(sketch, "E61.bottom", {"start": v(42.85, -24.16) * mm, "end": v(48.85, -24.16) * mm});
            skLineSegment(sketch, "E61.top", {"start": v(42.85, -27.16) * mm, "end": v(48.85, -27.16) * mm});
            skLineSegment(sketch, "E61.left", {"start": v(42.85, -24.16) * mm, "end": v(42.85, -27.16) * mm});
            skLineSegment(sketch, "E61.right", {"start": v(48.85, -24.16) * mm, "end": v(48.85, -27.16) * mm});
            skSolve(sketch);
        }
        {
            var Q0;
            {var subQ0=sQuery(id+"F53.wireOp",EDGE,"E60.top");Q0=makeQuery(id+"F53.imprint","IMPRINT",FACE,{"disambiguationData":[TD([[makeQuery(id+"F53.imprint","IMPRINT",EDGE,{"derivedFrom":subQ0}),1.0]])]});}
            var Q1;
            {var subQ0=sQuery(id+"F53.wireOp",EDGE,"E60.bottom");Q1=makeQuery(id+"F53.imprint","IMPRINT",FACE,{"disambiguationData":[TD([[makeQuery(id+"F53.imprint","IMPRINT",EDGE,{"derivedFrom":subQ0}),-1.0]])]});}
            extrude(context, id + "F54", {"entities" : qUnion([Q0, Q1]), "operationType" : NewBodyOperationType.ADD, "depth" : 2 * mm, "offsetDistance" : 25 * mm});
        }
        {
            var Q0;
            Q0=makeQuery(id+"F54.opExtrude","CAP_EDGE",EDGE,{"disambiguationData":[OSD([sQuery(id+"F53.wireOp",EDGE,"E60.top")])],"isStart":false});
            chamfer(context, id + "F55", {"entities" : qUnion([Q0]), "chamferType" : ChamferType.OFFSET_ANGLE, "width" : 1.5 * mm, "oppositeDirection" : false, "angle" : 50 * degree, "tangentPropagation" : true});
        }
        {
            var Q0;
            Q0=makeQuery(id+"F48.imprint","IMPRINT",FACE,{"disambiguationData":[TD([[makeQuery(id+"F48.imprint","IMPRINT",EDGE,{"derivedFrom":sQuery(id+"F48.wireOp",EDGE,"E58.bottom")}),-1.0]])]});
            extrude(context, id + "F56", {"entities" : qUnion([Q0]), "operationType" : NewBodyOperationType.REMOVE, "oppositeDirection" : true, "depth" : 3 * mm, "offsetDistance" : 25 * mm});
        }
        {
            var Q0;
            Q0=makeQuery(id+"F53.imprint","IMPRINT",FACE,{"disambiguationData":[TD([[makeQuery(id+"F53.imprint","IMPRINT",EDGE,{"derivedFrom":sQuery(id+"F53.wireOp",EDGE,"E61.bottom")}),-1.0]])]});
            extrude(context, id + "F57", {"entities" : qUnion([Q0]), "operationType" : NewBodyOperationType.ADD, "depth" : 2 * mm, "offsetDistance" : 25 * mm});
        }
        {
            var Q0;
            Q0=makeQuery(id+"F57.opExtrude","CAP_EDGE",EDGE,{"disambiguationData":[OSD([sQuery(id+"F53.wireOp",EDGE,"E61.bottom")])],"isStart":false});
            chamfer(context, id + "F58", {"entities" : qUnion([Q0]), "chamferType" : ChamferType.OFFSET_ANGLE, "width" : 1.5 * mm, "oppositeDirection" : false, "angle" : 50 * degree, "tangentPropagation" : true});
        }
        {
            var Q0;
            Q0=makeQuery(id+"F17.imprint","IMPRINT",FACE,{"disambiguationData":[TD([[makeQuery(id+"F17.imprint","IMPRINT",EDGE,{"derivedFrom":sQuery(id+"F17.wireOp",EDGE,"E27.bottom")}),-1.0]])]});
            extrude(context, id + "F59", {"entities" : qUnion([Q0]), "operationType" : NewBodyOperationType.ADD, "depth" : 6.5 * mm, "offsetDistance" : 25 * mm});
        }
        {
            var Q0;
            Q0=makeQuery(id+"F59.opExtrude","CAP_FACE",FACE,{"disambiguationData":[OSD([sQuery(id+"F17.wireOp",EDGE,"E27.bottom"),sQuery(id+"F17.wireOp",EDGE,"E27.top"),sQuery(id+"F17.wireOp",EDGE,"E27.left"),sQuery(id+"F17.wireOp",EDGE,"E27.right")])],"isStart":false});
            var sketch = newSketch(context, id + "F60", { "sketchPlane" : qUnion([Q0])});
            skLineSegment(sketch, "E62.bottom", {"start": v(-0.96, -29.5) * mm, "end": v(2.04, -29.5) * mm});
            skLineSegment(sketch, "E62.top", {"start": v(-0.96, -23.5) * mm, "end": v(2.04, -23.5) * mm});
            skLineSegment(sketch, "E62.left", {"start": v(-0.96, -29.5) * mm, "end": v(-0.96, -23.5) * mm});
            skLineSegment(sketch, "E62.right", {"start": v(2.04, -29.5) * mm, "end": v(2.04, -23.5) * mm});
            skSolve(sketch);
        }
        {
            var Q0;
            Q0=makeQuery(id+"F60.imprint","IMPRINT",FACE,{"disambiguationData":[TD([[makeQuery(id+"F60.imprint","IMPRINT",EDGE,{"derivedFrom":sQuery(id+"F60.wireOp",EDGE,"E62.top")}),-1.0]])]});
            var Q1;
            {var subQ5=makeQuery(id+"F59.opExtrude","CAP_EDGE",EDGE,{"disambiguationData":[OSD([sQuery(id+"F17.wireOp",EDGE,"E27.left")])],"isStart":false});Q1=makeQuery(id+"F60.imprint","IMPRINT",FACE,{"disambiguationData":[TD([[makeQuery(id+"F60.imprint","IMPRINT",EDGE,{"derivedFrom":subQ5}),1.0]])]});}
            extrude(context, id + "F61", {"entities" : qUnion([Q0, Q1]), "operationType" : NewBodyOperationType.ADD, "depth" : 2 * mm, "offsetDistance" : 25 * mm});
        }
        {
            var Q0;
            Q0=makeQuery(id+"F61.opExtrude","CAP_EDGE",EDGE,{"disambiguationData":[OSD([sQuery(id+"F60.wireOp",EDGE,"E62.left")])],"isStart":false});
            chamfer(context, id + "F62", {"entities" : qUnion([Q0]), "chamferType" : ChamferType.OFFSET_ANGLE, "width" : 1.5 * mm, "oppositeDirection" : true, "angle" : 50 * degree, "tangentPropagation" : true});
        }
    });
